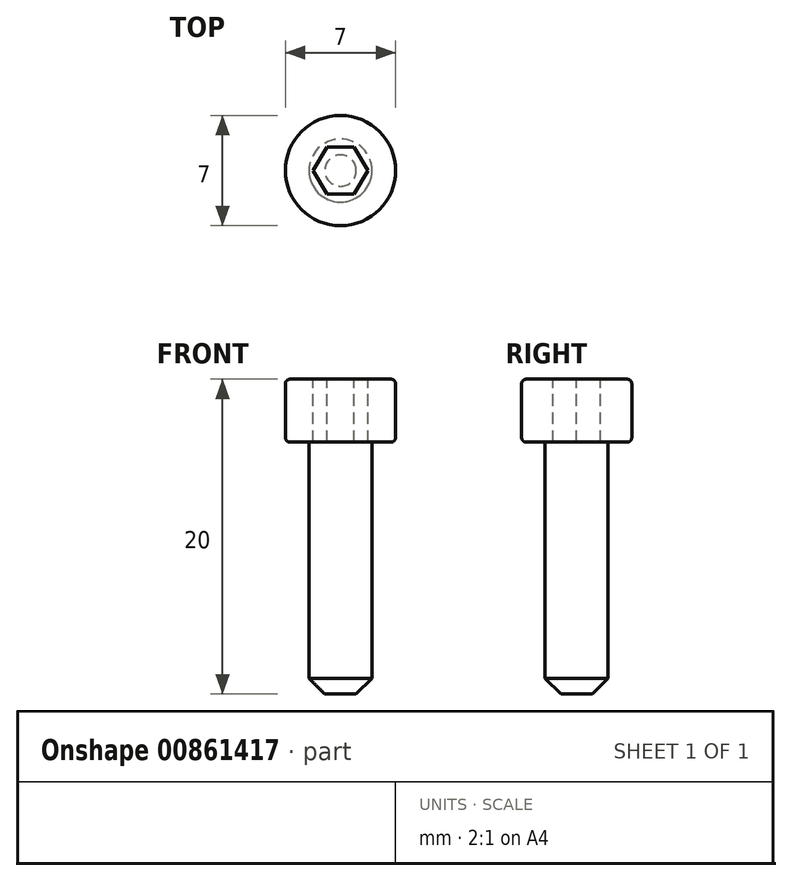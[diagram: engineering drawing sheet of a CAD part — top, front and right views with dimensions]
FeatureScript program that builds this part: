
annotation { "Feature Type Name" : "Feature", "Feature Type Description" : "" }
export const myFeature = defineFeature(function(context is Context, id is Id, definition is map)
    precondition{}
    {
        {
            var Q0;
            Q0=qCreatedBy(makeId("Front.planeOp"),FACE);
            var sketch = newSketch(context, id + "F0", { "sketchPlane" : qUnion([Q0])});
            skLineSegment(sketch, "E0", {"start": v(0, 4) * mm, "end": v(3.5, 4) * mm});
            skLineSegment(sketch, "E1", {"start": v(3.5, 4) * mm, "end": v(3.5, 0) * mm});
            skLineSegment(sketch, "E2", {"start": v(3.5, 0) * mm, "end": v(2, 0) * mm});
            skLineSegment(sketch, "E3", {"start": v(2, 0) * mm, "end": v(2, -16) * mm});
            skLineSegment(sketch, "E4", {"start": v(2, -16) * mm, "end": v(0, -16) * mm});
            skLineSegment(sketch, "E5", {"start": v(0, -16) * mm, "end": v(0, 4) * mm});
            skLineSegment(sketch, "E6", {"start": v(0, 32.65) * mm, "end": v(0, -133.76) * mm, "construction": true});
            skSolve(sketch);
        }
        {
            var Q0;
            Q0=makeQuery(id+"F0.imprint","IMPRINT",FACE,{"disambiguationData":[TD([[makeQuery(id+"F0.imprint","IMPRINT",EDGE,{"derivedFrom":sQuery(id+"F0.wireOp",EDGE,"E0")}),-1.0]])]});
            var Q1;
            Q1=sQuery(id+"F0.wireOp",EDGE,"E6");
            var Q2;
            Q2=sQuery(id+"F0.wireOp",EDGE,"E6");
            revolve(context, id + "F1", {"surfaceOperationType" : NewSurfaceOperationType.NEW, "entities" : qUnion([Q0]), "surfaceEntities" : qUnion([Q1]), "axis" : qUnion([Q2]), "revolveType" : RevolveType.FULL});
        }
        {
            var Q0;
            Q0=makeQuery(id+"F1.opRevolve","SWEPT_FACE",FACE,{"disambiguationData":[OSD([sQuery(id+"F0.wireOp",EDGE,"E0")])]});
            var sketch = newSketch(context, id + "F2", { "sketchPlane" : qUnion([Q0])});
            skCircle(sketch, "E7.cCircle", {"center": v(0, 0) * mm, "radius": 1.5 * mm, "construction": true});
            skLineSegment(sketch, "E7.0", {"start": v(-0.87, 1.5) * mm, "end": v(0.87, 1.5) * mm});
            skLineSegment(sketch, "E7.1", {"start": v(0.87, 1.5) * mm, "end": v(1.73, 0) * mm});
            skLineSegment(sketch, "E7.2", {"start": v(1.73, 0) * mm, "end": v(0.87, -1.5) * mm});
            skLineSegment(sketch, "E7.3", {"start": v(0.87, -1.5) * mm, "end": v(-0.87, -1.5) * mm});
            skLineSegment(sketch, "E7.4", {"start": v(-0.87, -1.5) * mm, "end": v(-1.73, 0) * mm});
            skLineSegment(sketch, "E7.5", {"start": v(-1.73, 0) * mm, "end": v(-0.87, 1.5) * mm});
            skPoint(sketch, "E7.0.midPoint", {"position": v(0, 1.5) * mm});
            skSolve(sketch);
        }
        {
            var Q0;
            Q0=qSketchRegion(id+"F2",true);
            extrude(context, id + "F3", {"entities" : qUnion([Q0]), "operationType" : NewBodyOperationType.REMOVE, "oppositeDirection" : true, "depth" : 4 * mm, "offsetDistance" : 25 * mm});
        }
        {
            var Q0;
            Q0=makeQuery(id+"F1.opRevolve","SWEPT_EDGE",EDGE,{"disambiguationData":[OSD([sQuery(id+"F0.wireOp",EDGE,"E3"),sQuery(id+"F0.wireOp",EDGE,"E4")])]});
            chamfer(context, id + "F4", {"entities" : qUnion([Q0]), "width" : 1 * mm, "tangentPropagation" : true});
        }
        {
            var Q0;
            Q0=makeQuery(id+"F1.opRevolve","SWEPT_EDGE",EDGE,{"disambiguationData":[OSD([sQuery(id+"F0.wireOp",EDGE,"E1"),sQuery(id+"F0.wireOp",EDGE,"E2")])]});
            var Q1;
            Q1=makeQuery(id+"F1.opRevolve","SWEPT_EDGE",EDGE,{"disambiguationData":[OSD([sQuery(id+"F0.wireOp",EDGE,"E0"),sQuery(id+"F0.wireOp",EDGE,"E1")])]});
            fillet(context, id + "F5", {"entities" : qUnion([Q0, Q1]), "radius" : 0.3 * mm, "tangentPropagation" : true, "allowEdgeOverflow" : false});
        }
    });
